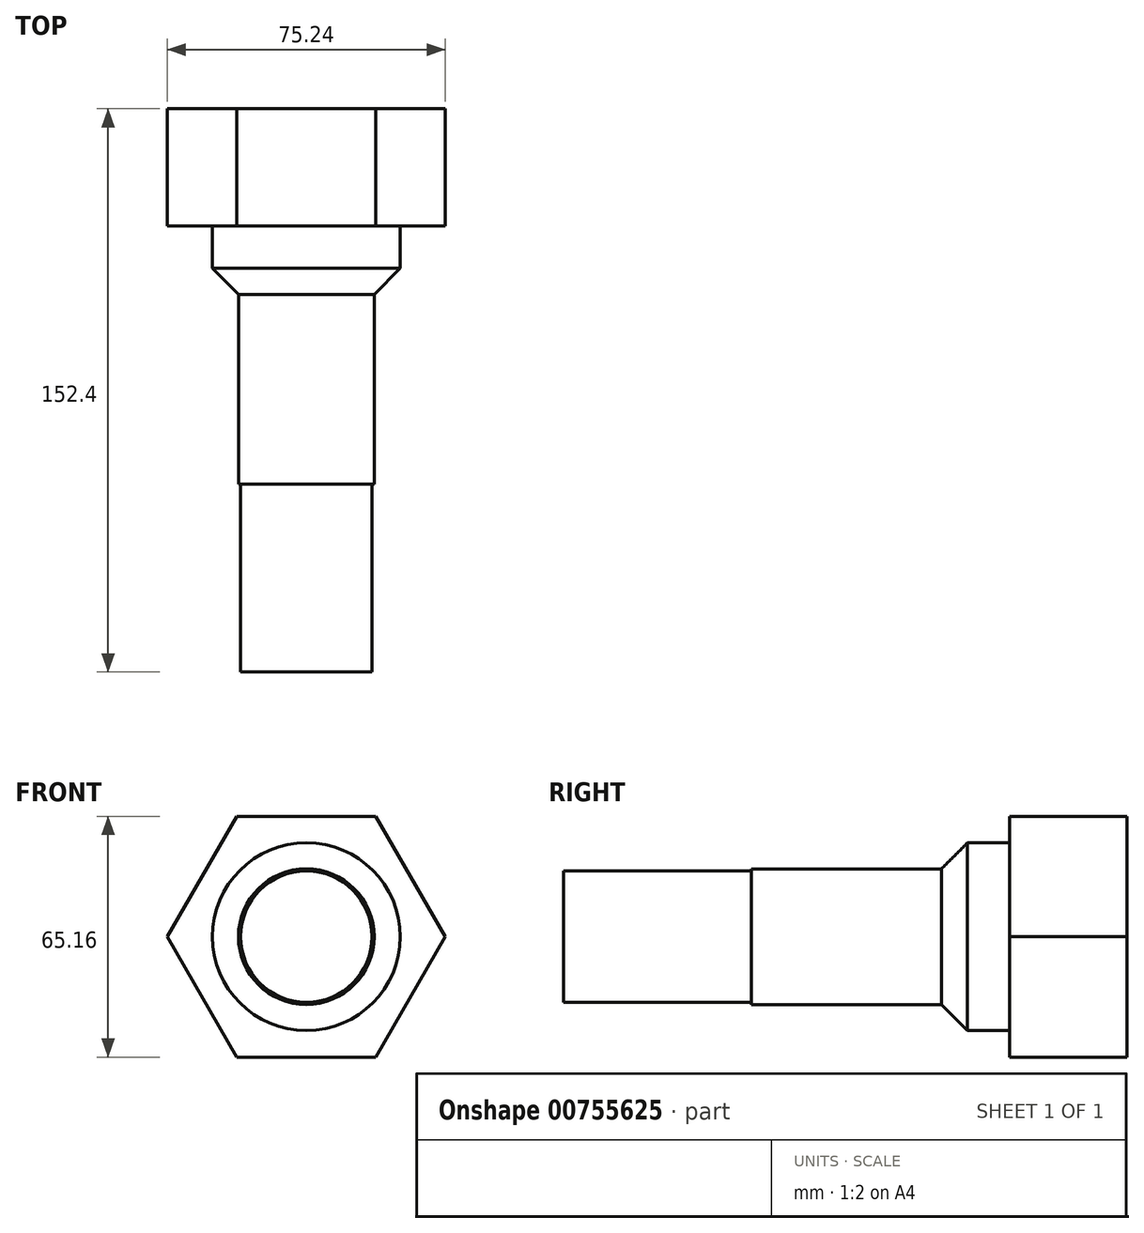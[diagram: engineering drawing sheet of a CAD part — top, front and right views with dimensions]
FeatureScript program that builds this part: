
annotation { "Feature Type Name" : "Feature", "Feature Type Description" : "" }
export const myFeature = defineFeature(function(context is Context, id is Id, definition is map)
    precondition{}
    {
        {
            var Q0;
            Q0=qCreatedBy(makeId("Front.planeOp"),FACE);
            var sketch = newSketch(context, id + "F0", { "sketchPlane" : qUnion([Q0])});
            skCircle(sketch, "E0.cCircle", {"center": v(0, 0) * mm, "radius": 32.58 * mm, "construction": true});
            skLineSegment(sketch, "E0.0", {"start": v(18.8, -32.58) * mm, "end": v(-18.8, -32.58) * mm});
            skLineSegment(sketch, "E0.1", {"start": v(-18.8, -32.58) * mm, "end": v(-37.62, 0) * mm});
            skLineSegment(sketch, "E0.2", {"start": v(-37.62, 0) * mm, "end": v(-18.8, 32.58) * mm});
            skLineSegment(sketch, "E0.3", {"start": v(-18.8, 32.58) * mm, "end": v(18.8, 32.58) * mm});
            skLineSegment(sketch, "E0.4", {"start": v(18.8, 32.58) * mm, "end": v(37.62, 0) * mm});
            skLineSegment(sketch, "E0.5", {"start": v(37.62, 0) * mm, "end": v(18.8, -32.58) * mm});
            skPoint(sketch, "E0.0.midPoint", {"position": v(0, -32.58) * mm});
            skSolve(sketch);
        }
        {
            var Q0;
            Q0 = qSketchRegion(id + "F0", true);
            extrude(context, id + "F1", {"entities" : qUnion([Q0]), "depth" : 31.75 * mm, "offsetDistance" : 25.4 * mm});
        }
        {
            var Q0;
            Q0=qCreatedBy(makeId("Front.planeOp"),FACE);
            var sketch = newSketch(context, id + "F2", { "sketchPlane" : qUnion([Q0])});
            skCircle(sketch, "E1", {"center": v(0, 0) * mm, "radius": 25.4 * mm});
            skSolve(sketch);
        }
        {
            var Q0;
            Q0 = qSketchRegion(id + "F2", true);
            extrude(context, id + "F3", {"entities" : qUnion([Q0]), "operationType" : NewBodyOperationType.ADD, "depth" : 50.8 * mm, "offsetDistance" : 25.4 * mm});
        }
        {
            var Q0;
            Q0=makeQuery(id+"F3.opExtrude","CAP_EDGE",EDGE,{"disambiguationData":[OSD([sQuery(id+"F2.wireOp",EDGE,"E1")])],"isStart":false});
            chamfer(context, id + "F4", {"entities" : qUnion([Q0]), "width" : 7.62 * mm, "tangentPropagation" : true});
        }
        {
            var Q0;
            Q0=qCreatedBy(makeId("Front.planeOp"),FACE);
            var sketch = newSketch(context, id + "F5", { "sketchPlane" : qUnion([Q0])});
            skCircle(sketch, "E2", {"center": v(0, 0) * mm, "radius": 18.36 * mm});
            skSolve(sketch);
        }
        {
            var Q0;
            Q0 = qSketchRegion(id + "F5", true);
            var Q1;
            Q1=makeQuery(id+"F3.opExtrude","CAP_FACE",FACE,{"disambiguationData":[OSD([sQuery(id+"F2.wireOp",EDGE,"E1")])],"isStart":false});
            extrude(context, id + "F6", {"entities" : qUnion([Q0, Q1]), "operationType" : NewBodyOperationType.ADD, "depth" : 101.6 * mm, "offsetDistance" : 25.4 * mm});
        }
    });
